# Revit family: 0048935
name_source: partatom
category: Lighting Fixtures
revit_build: Autodesk Revit 2017 (Build: 20190507_1515(x64)
units: mm (PartAtom-declared; Revit-internal decimal feet)

## family parameters
Cut with Voids When Loaded = No
Host = Face
Light Source = Yes
OmniClass Number = 23.80.70.00
OmniClass Title = Lighting
Part Type = Normal
Room Calculation Point = No
Round Connector Dimension = Use Diameter
Shared = No

## types (8) — shared parameters
Assembly Code = D5020200
AssetType = Fixed
ClassificationName = Uniclass2015
ClassificationValue = EF_70_80
Color Filter = 16777215
Default Elevation = 1219 mm
Dimming Lamp Color Temperature Shift = <None>
DocumentationLiterature = http://www.sylvania-lighting.com
ElectricShockClassification = Class I
Emit Shape Visible in Rendering = No
Emit from Circle Diameter = 610 mm
GAP_SYL = 3 mm  [stored 0.00984252 ft]
HEIGHT_SYL = 77 mm
HOLE_HEIGHT_SYL = 24 mm
IfcExportAs = IfcLightFixtureType
IfcExportType = IfcLightFixtureType
ImpactProtectionIndex = IK08
IngressProtection = IP20
Keynote = 16500
LUM_R_SYL = 30 mm  [stored 0.0984252 ft]
Lamp = LED
LampColourRenderingIndex = 80
LampColourTemperature = 4000 K
LampMacAdamStep = 5
LampsType = LED
Manufacturer = Feilo Sylvania
ManufacturerName = Feilo Sylvania
Material = steel housing, pc polycarbonate diffuser
Material_1_SYL = Dynamo
Material_2_SYL = <By Category>
Material_3_SYL = <By Category>
Material_4_SYL = <By Category>
NominalDepth = 70 mm
NominalHeight = 77 mm
NominalLength = 1523 mm
R_HEIGHT_SYL = 44 mm
Tilt Angle = -90.00°
Type Image = <None>
URL = http://www.sylvania-lighting.com
Voltage = 0 V
WIDTH/2_SYL = 35 mm  [stored 0.114829 ft]
zero-valued in all types: Cost

## per-type parameters (varying)
| type | Apparent Load | Description | LampNominalLuminous | LuminousEfficacy | Model | ModelNumber | ModelReference | Name | Photometric Web File | PowerConsumption | PowerFactor | TypeName | Weight |
| 0048954 WAYLINE 1500 MWCOR 5200LM 840 | 38 VA | LED batten, T8 replacement, ease of installation through 2 part push-in design of the housing (safety cable included), through wiring capability, steel housing, 5200lm, 38W, 137lm/W, 4000K, CRI80, 3 step MacAdam ellipse, symmetric wide beam angle, Class I, 90000 hrs L80B20 lifespan, non-dimmable driver, corridor function with microwave presence sensor, IK08, IP20, 1523 x 70 x 76.5mm  (L x W x H) dimensions, 2.07kg. | 5200 lm | 137 lm/W | Wayline 1500 MWCOR 5200lm 840 | 48954 | Wayline 1500 MWCOR 5200lm 840 | Wayline 1500 MWCOR 5200lm 840 | 0048954.ies | 38 W | 0.9 | Wayline 1500 MWCOR 5200lm 840 | 8.28 kg |
| 0048935 WAYLINE 1500 MW 8400LM 840 | 61 VA | LED batten, T8 replacement, ease of installation through 2 part push-in design of the housing (safety cable included), through wiring capability, steel housing, 8400lm, 61W, 138lm/W, 4000K, CRI80, 3 step MacAdam ellipse, symmetric wide beam angle, Class I, 90000 hrs L80B20 lifespan, non-dimmable driver, MW sensor for 360° detection up to 8m range at 6m mounting height, IK08, IP20, 1523 x 70 x 76.5mm (LxWxD) dimensions, 1.94kg weight. | 8400 lm | 138 lm/W | Wayline 1500 MW 8400lm 840 | 48935 | Wayline 1500 MW 8400lm 840 | Wayline 1500 MW 8400lm 840 | 0048935.ies | 61 W | 0.9 | Wayline 1500 MW 8400lm 840 | 7.76 kg |
| 0048934 WAYLINE 1500 MW 5200LM 840 | 37 VA | LED batten, T8 replacement, ease of installation through 2 part push-in design of the housing (safety cable included), through wiring capability, steel housing, 5200lm, 37W, 141lm/W, 4000K, CRI80, 3 step MacAdam ellipse, symmetric wide beam angle, Class I, 90000 hrs L80B20 lifespan, non-dimmable driver, MW sensor for 360° detection up to 8m range at 6m mounting height, IK08, IP20, 1523 x 70 x 76.5mm (LxWxD) dimensions, 1.79kg weight. | 5200 lm | 141 lm/W | Wayline 1500 MW 5200lm 840 | 48934 | Wayline 1500 MW 5200lm 840 | Wayline 1500 MW 5200lm 840 | 0048934.ies | 37 W | 0.9 | Wayline 1500 MW 5200lm 840 | 7.16 kg |
| 0048931 WAYLINE 1500 8400LM 840 EM | 64 VA | LED batten, T8 replacement, ease of installation through 2 part push-in design of the housing (safety cable included), through wiring capability, steel housing, 8400lm, 64W, 131lm/W, 4000K, CRI80, 3 step MacAdam ellipse, symmetric wide beam angle, Class I, 90000 hrs L80B20 lifespan, non-dimmable driver, 3-hour maintained emergency batteries, IK08, IP20, 1523 x 70 x 76.5mm  (L x W x H) dimensions, 2.29kg. | 8400 lm | 131 lm/W | Wayline 1500 8400lm 840 EM | 48931 | Wayline 1500 8400lm 840 EM | Wayline 1500 8400lm 840 EM | 0048931.ies | 64 W | 1 | Wayline 1500 8400lm 840 EM | 9.16 kg |
| 0048930 WAYLINE 1500 5200LM 840 EM | 41 VA | LED batten, T8 replacement, ease of installation through 2 part push-in design of the housing (safety cable included), through wiring capability, steel housing, 5200lm, 41W, 127lm/W, 4000K, CRI80, 3 step MacAdam ellipse, symmetric wide beam angle, Class I, 90000 hrs L80B20 lifespan, non-dimmable driver, 3-hour maintained emergency batteries, IK08, IP20, 1523 x 70 x 76.5mm  (L x W x H) dimensions, 2.14kg. | 5200 lm | 127 lm/W | Wayline 1500 5200lm 840 EM | 48930 | Wayline 1500 5200lm 840 EM | Wayline 1500 5200lm 840 EM | 0048930.ies | 41 W | 1 | Wayline 1500 5200lm 840 EM | 8.56 kg |
| 0048927 WAYLINE 1500 DALI 8300LM 840 | 60 VA | LED batten, T8 replacement, ease of installation through 2 part push-in design of the housing (safety cable included), through wiring capability, steel housing, 8300lm, 60W, 138lm/W, 4000K, CRI80, 3 step MacAdam ellipse, symmetric wide beam angle, Class I, 90000 hrs L80B20 lifespan, DALI dimmable driver, IK08, IP20, 1523 x 70 x 76.5mm (LxWxD) dimensions, 2kg weight. | 8300 lm | 138 lm/W | Wayline 1500 DALI 8300lm 840 | 48927 | Wayline 1500 DALI 8300lm 840 | Wayline 1500 DALI 8300lm 840 | 0048927.ies | 60 W | 0.9 | Wayline 1500 DALI 8300lm 840 | 8.0 kg |
| 0048926 WAYLINE 1500 DALI 5200LM 840 | 37 VA | LED batten, T8 replacement, ease of installation through 2 part push-in design of the housing (safety cable included), through wiring capability, steel housing, 5200lm, 37W, 141lm/W, 4000K, CRI80, 3 step MacAdam ellipse, symmetric wide beam angle, Class I, 90000 hrs L80B20 lifespan, DALI dimmable driver, IK08, IP20, 1523 x 70 x 76.5mm (LxWxD) dimensions, 2kg weight. | 5200 lm | 141 lm/W | Wayline 1500 DALI 5200lm 840 | 48926 | Wayline 1500 DALI 5200lm 840 | Wayline 1500 DALI 5200lm 840 | 0048926.ies | 37 W | 0.9 | Wayline 1500 DALI 5200lm 840 | 8.0 kg |
| 0048955 WAYLINE 1500 MWCOR 8300LM 840 | 61 VA | LED batten, T8 replacement, ease of installation through 2 part push-in design of the housing (safety cable included), through wiring capability, steel housing, 8300lm, 61W, 136lm/W, 4000K, CRI80, 3 step MacAdam ellipse, symmetric wide beam angle, Class I, 90000 hrs L80B20 lifespan, non-dimmable driver, corridor function with microwave presence sensor, IK08, IP20, 1523 x 70 x 76.5mm  (L x W x H) dimensions, 2.07kg. | 8300 lm | 136 lm/W | Wayline 1500 MWCOR 8300lm 840 | 48955 | Wayline 1500 MWCOR 8300lm 840 | Wayline 1500 MWCOR 8300lm 840 | 0048955.ies | 61 W | 0.9 | Wayline 1500 MWCOR 8300lm 840 | 8.28 kg |

note: [stored X ft] marks values corroborated as IEEE doubles in the binary element streams (Revit-internal decimal feet)

## geometry (parser evidence)
native form markers: Sweep x3
no freeform markers — native parametric forms only
